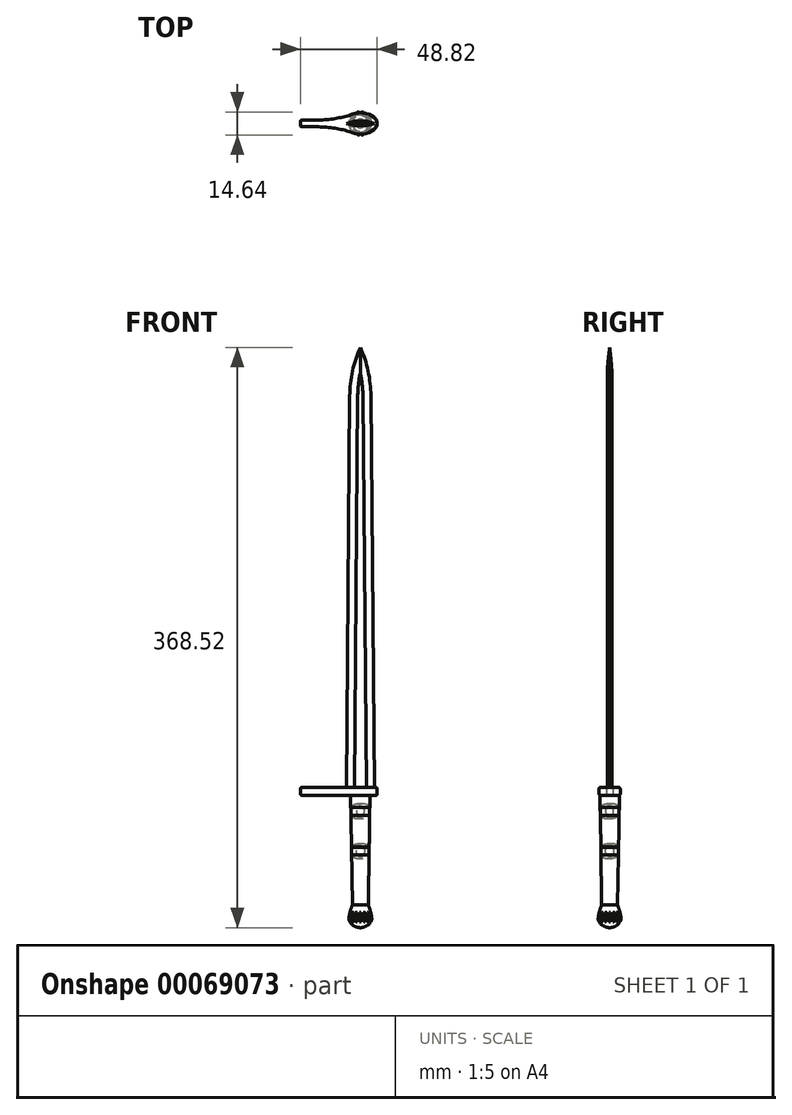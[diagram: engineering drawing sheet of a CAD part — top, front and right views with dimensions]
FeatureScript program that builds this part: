
annotation { "Feature Type Name" : "Feature", "Feature Type Description" : "" }
export const myFeature = defineFeature(function(context is Context, id is Id, definition is map)
    precondition{}
    {
        {
            var Q0;
            Q0=qCreatedBy(makeId("Right.planeOp"),FACE);
            var sketch = newSketch(context, id + "F0", { "sketchPlane" : qUnion([Q0])});
            skLineSegment(sketch, "E0", {"start": v(0, 0) * mm, "end": v(-6.1, 0) * mm});
            skLineSegment(sketch, "E1", {"start": v(0, 0) * mm, "end": v(0, -52.88) * mm});
            skLineSegment(sketch, "E2", {"start": v(0, 0) * mm, "end": v(6.1, 0) * mm});
            skPoint(sketch, "E3.end.orphan", {"position": v(-6.1, 0) * mm});
            skLineSegment(sketch, "E4", {"start": v(0, -52.88) * mm, "end": v(0, -69.72) * mm});
            skLineSegment(sketch, "E5", {"start": v(0, -69.72) * mm, "end": v(-5.08, -69.72) * mm});
            skLineSegment(sketch, "E6.MirrorCS", {"start": v(0, -69.72) * mm, "end": v(5.08, -69.72) * mm});
            skLineSegment(sketch, "E7", {"start": v(-5.08, -69.72) * mm, "end": v(-6.1, 0) * mm});
            skLineSegment(sketch, "E8", {"start": v(5.08, -69.72) * mm, "end": v(6.1, 0) * mm});
            skArc(sketch, "E9", {"start": v(-5.98, -7.62) * mm, "mid": v(-6.68, -10.11) * mm, "end": v(-5.91, -12.59) * mm});
            skLineSegment(sketch, "E10", {"start": v(-5.58, -35.4) * mm, "end": v(-13.44, -35.51) * mm});
            skArc(sketch, "E11.MirrorCS", {"start": v(-5.18, -63.18) * mm, "mid": v(-5.94, -60.7) * mm, "end": v(-5.25, -58.2) * mm});
            skLineSegment(sketch, "E12", {"start": v(-2.07, -10.05) * mm, "end": v(-5.91, -10.1) * mm});
            skLineSegment(sketch, "E13", {"start": v(-5.75, -22.75) * mm, "end": v(-5.91, -10.1) * mm});
            skPoint(sketch, "E14", {"position": v(-5.75, -22.75) * mm});
            skLineSegment(sketch, "E15", {"start": v(-5.75, -22.75) * mm, "end": v(-9.83, -22.8) * mm});
            skArc(sketch, "E16.MirrorCS", {"start": v(-5.59, -37.88) * mm, "mid": v(-6.34, -35.4) * mm, "end": v(-5.65, -32.91) * mm});
            skLineSegment(sketch, "E17", {"start": v(-5.59, -37.88) * mm, "end": v(-5.54, -37.95) * mm});
            skLineSegment(sketch, "E18", {"start": v(-5.65, -32.91) * mm, "end": v(-5.62, -32.87) * mm});
            skSolve(sketch);
        }
        {
            var Q0;
            {var subQ8=sQuery(id+"F0.wireOp",EDGE,"E0");Q0=makeQuery(id+"F0.imprint","IMPRINT",FACE,{"disambiguationData":[TD([[makeQuery(id+"F0.imprint","IMPRINT",EDGE,{"derivedFrom":subQ8}),1.0]])]});}
            var Q1;
            Q1=sQuery(id+"F0.wireOp",EDGE,"E1");
            revolve(context, id + "F1", {"entities" : qUnion([Q0]), "axis" : qUnion([Q1]), "revolveType" : RevolveType.FULL});
        }
        {
            var Q0;
            {var subQ3=sQuery(id+"F0.wireOp",EDGE,"E18");Q0=makeQuery(id+"F0.imprint","IMPRINT",FACE,{"disambiguationData":[TD([[makeQuery(id+"F0.imprint","IMPRINT",EDGE,{"derivedFrom":subQ3}),-1.0]])]});}
            var Q1;
            {var subQ3=sQuery(id+"F0.wireOp",EDGE,"E17");Q1=makeQuery(id+"F0.imprint","IMPRINT",FACE,{"disambiguationData":[TD([[makeQuery(id+"F0.imprint","IMPRINT",EDGE,{"derivedFrom":subQ3}),1.0]])]});}
            var Q2;
            {var subQ0=sQuery(id+"F0.wireOp",EDGE,"E9");Q2=makeQuery(id+"F0.imprint","IMPRINT",FACE,{"disambiguationData":[TD([[makeQuery(id+"F0.imprint","IMPRINT",EDGE,{"derivedFrom":subQ0}),1.0]])]});}
            var Q3;
            {var subQ0=sQuery(id+"F0.wireOp",EDGE,"E11.MirrorCS");Q3=makeQuery(id+"F0.imprint","IMPRINT",FACE,{"disambiguationData":[TD([[makeQuery(id+"F0.imprint","IMPRINT",EDGE,{"derivedFrom":subQ0}),-1.0]])]});}
            var Q4;
            Q4=sQuery(id+"F0.wireOp",EDGE,"E4");
            revolve(context, id + "F2", {"entities" : qUnion([Q0, Q1, Q2, Q3]), "axis" : qUnion([Q4]), "revolveType" : RevolveType.FULL});
        }
        {
            var Q0;
            Q0=makeQuery(id+"F1.opRevolve","SWEPT_FACE",FACE,{"disambiguationData":[OSD([sQuery(id+"F0.wireOp",EDGE,"E0")])]});
            var sketch = newSketch(context, id + "F3", { "sketchPlane" : qUnion([Q0])});
            skEllipse(sketch, "E19", {"center": v(0, 0) * mm, "majorRadius": 6.74 * mm, "minorRadius": 10.7 * mm, "majorAxis": v(0, 1)});
            skLineSegment(sketch, "E20", {"start": v(-10.7, 0) * mm, "end": v(-38.12, 0) * mm});
            skPoint(sketch, "E20.endSnap0", {"position": v(-10.7, 0) * mm});
            skLineSegment(sketch, "E21", {"start": v(-38.12, 0) * mm, "end": v(-38.12, 2.16) * mm});
            skLineSegment(sketch, "E22", {"start": v(-38.12, 2.16) * mm, "end": v(-27.96, 2.16) * mm});
            skArc(sketch, "E23", {"start": v(-27.96, 2.16) * mm, "mid": v(-17.38, 2.9) * mm, "end": v(-7, 5.1) * mm});
            skArc(sketch, "E24.MirrorCS", {"start": v(-27.96, -2.16) * mm, "mid": v(-17.38, -2.9) * mm, "end": v(-7, -5.1) * mm});
            skLineSegment(sketch, "E25.MirrorCS", {"start": v(-38.12, -2.16) * mm, "end": v(-27.96, -2.16) * mm});
            skLineSegment(sketch, "E26.MirrorCS", {"start": v(-38.12, 0) * mm, "end": v(-38.12, -2.16) * mm});
            skLineSegment(sketch, "E27", {"start": v(0, 0) * mm, "end": v(0, 3.03) * mm});
            skArc(sketch, "E28.MirrorCS", {"start": v(27.96, 2.16) * mm, "mid": v(17.38, 2.9) * mm, "end": v(7, 5.1) * mm});
            skArc(sketch, "E29.MirrorCS", {"start": v(27.96, -2.16) * mm, "mid": v(17.38, -2.9) * mm, "end": v(7, -5.1) * mm});
            skLineSegment(sketch, "E30.MirrorCS", {"start": v(38.12, 0) * mm, "end": v(38.12, -2.16) * mm});
            skLineSegment(sketch, "E31.MirrorCS", {"start": v(38.12, 0) * mm, "end": v(38.12, 2.16) * mm});
            skLineSegment(sketch, "E32.MirrorCS", {"start": v(38.12, 2.16) * mm, "end": v(27.96, 2.16) * mm});
            skLineSegment(sketch, "E33.MirrorCS", {"start": v(38.12, -2.16) * mm, "end": v(27.96, -2.16) * mm});
            skSolve(sketch);
        }
        {
            var Q0;
            {var subQ1=sQuery(id+"F3.wireOp",EDGE,"E20");Q0=makeQuery(id+"F3.imprint","IMPRINT",FACE,{"disambiguationData":[TD([[makeQuery(id+"F3.imprint","IMPRINT",EDGE,{"derivedFrom":subQ1}),-1.0]])]});}
            var Q1;
            {var subQ1=sQuery(id+"F3.wireOp",EDGE,"E20");Q1=makeQuery(id+"F3.imprint","IMPRINT",FACE,{"disambiguationData":[TD([[makeQuery(id+"F3.imprint","IMPRINT",EDGE,{"derivedFrom":subQ1}),1.0]])]});}
            var Q2;
            Q2=makeQuery(id+"F3.imprint","IMPRINT",FACE,{"disambiguationData":[TD([[makeQuery(id+"F3.imprint","IMPRINT",EDGE,{"derivedFrom":makeQuery(id+"F1.opRevolve","SWEPT_EDGE",EDGE,{"disambiguationData":[OSD([sQuery(id+"F0.wireOp",EDGE,"E0"),sQuery(id+"F0.wireOp",EDGE,"E7")])]})}),-1.0]])]});
            var Q3;
            {var subQ0=sQuery(id+"F3.wireOp",EDGE,"E28.MirrorCS");Q3=makeQuery(id+"F3.imprint","IMPRINT",FACE,{"disambiguationData":[TD([[makeQuery(id+"F3.imprint","IMPRINT",EDGE,{"derivedFrom":subQ0}),1.0]])]});}
            var Q4;
            Q4=makeQuery(id+"F3.imprint","IMPRINT",FACE,{"disambiguationData":[TD([[makeQuery(id+"F3.imprint","IMPRINT",EDGE,{"derivedFrom":makeQuery(id+"F1.opRevolve","SWEPT_EDGE",EDGE,{"disambiguationData":[OSD([sQuery(id+"F0.wireOp",EDGE,"E0"),sQuery(id+"F0.wireOp",EDGE,"E7")])]})}),1.0]])]});
            extrude(context, id + "F4", {"entities" : qUnion([Q0, Q1, Q2, Q3, Q4]), "depth" : 5.08 * mm});
        }
        {
            var Q0;
            Q0=makeQuery(id+"F4.opExtrude","CAP_EDGE",EDGE,{"disambiguationData":[OSD([sQuery(id+"F3.wireOp",EDGE,"E24.MirrorCS")])],"isStart":false});
            var Q1;
            Q1=makeQuery(id+"F4.opExtrude","CAP_EDGE",EDGE,{"disambiguationData":[OSD([sQuery(id+"F3.wireOp",EDGE,"E25.MirrorCS")])],"isStart":false});
            var Q2;
            Q2=makeQuery(id+"F4.opExtrude","CAP_EDGE",EDGE,{"disambiguationData":[OSD([sQuery(id+"F3.wireOp",EDGE,"E25.MirrorCS")])],"isStart":true});
            var Q3;
            Q3=makeQuery(id+"F4.opExtrude","CAP_EDGE",EDGE,{"disambiguationData":[OSD([sQuery(id+"F3.wireOp",EDGE,"E24.MirrorCS")])],"isStart":true});
            var Q4;
            Q4=makeQuery(id+"F4.opExtrude","CAP_EDGE",EDGE,{"disambiguationData":[OSD([sQuery(id+"F3.wireOp",EDGE,"E23")])],"isStart":true});
            var Q5;
            Q5=makeQuery(id+"F4.opExtrude","CAP_EDGE",EDGE,{"disambiguationData":[OSD([sQuery(id+"F3.wireOp",EDGE,"E23")])],"isStart":false});
            var Q6;
            Q6=makeQuery(id+"F4.opExtrude","CAP_EDGE",EDGE,{"disambiguationData":[OSD([sQuery(id+"F3.wireOp",EDGE,"E22")])],"isStart":false});
            var Q7;
            Q7=makeQuery(id+"F4.opExtrude","SWEPT_EDGE",EDGE,{"disambiguationData":[OSD([sQuery(id+"F3.wireOp",EDGE,"E25.MirrorCS"),sQuery(id+"F3.wireOp",EDGE,"E26.MirrorCS")])]});
            var Q8;
            Q8=makeQuery(id+"F4.opExtrude","SWEPT_EDGE",EDGE,{"disambiguationData":[OSD([sQuery(id+"F3.wireOp",EDGE,"E21"),sQuery(id+"F3.wireOp",EDGE,"E22")])]});
            var Q9;
            Q9=makeQuery(id+"F4.opExtrude","CAP_EDGE",EDGE,{"disambiguationData":[OSD([sQuery(id+"F3.wireOp",EDGE,"E21"),sQuery(id+"F3.wireOp",EDGE,"E26.MirrorCS")])],"isStart":true});
            var Q10;
            Q10=makeQuery(id+"F4.opExtrude","CAP_EDGE",EDGE,{"disambiguationData":[OSD([sQuery(id+"F3.wireOp",EDGE,"E21"),sQuery(id+"F3.wireOp",EDGE,"E26.MirrorCS")])],"isStart":false});
            var Q11;
            Q11=makeQuery(id+"F4.opExtrude","CAP_EDGE",EDGE,{"disambiguationData":[OSD([sQuery(id+"F3.wireOp",EDGE,"E29.MirrorCS")])],"isStart":false});
            var Q12;
            Q12=makeQuery(id+"F4.opExtrude","CAP_EDGE",EDGE,{"disambiguationData":[OSD([sQuery(id+"F3.wireOp",EDGE,"E29.MirrorCS")])],"isStart":true});
            var Q13;
            Q13=makeQuery(id+"F4.opExtrude","CAP_EDGE",EDGE,{"disambiguationData":[OSD([sQuery(id+"F3.wireOp",EDGE,"E28.MirrorCS")])],"isStart":false});
            var Q14;
            Q14=makeQuery(id+"F4.opExtrude","CAP_EDGE",EDGE,{"disambiguationData":[OSD([sQuery(id+"F3.wireOp",EDGE,"E28.MirrorCS")])],"isStart":true});
            var Q15;
            Q15=makeQuery(id+"F4.opExtrude","SWEPT_FACE",FACE,{"disambiguationData":[OSD([sQuery(id+"F3.wireOp",EDGE,"E30.MirrorCS"),sQuery(id+"F3.wireOp",EDGE,"E31.MirrorCS")])]});
            var Q16;
            {var subQ0=sQuery(id+"F3.wireOp",EDGE,"E19");Q16=makeQuery(id+"F4.opExtrude","SWEPT_FACE",FACE,{"disambiguationData":[OSD([subQ0]),TDD([makeQuery(id+"F3.imprint","IMPRINT",EDGE,{"disambiguationData":[TD([[makeQuery(id+"F3.imprint","INTERSECT",VERTEX,{"derivedFrom":[subQ0,sQuery(id+"F3.wireOp",EDGE,"E24.MirrorCS")]}),-1.0]])],"derivedFrom":subQ0})])]});}
            var Q17;
            {var subQ0=sQuery(id+"F3.wireOp",EDGE,"E19");Q17=makeQuery(id+"F4.opExtrude","SWEPT_FACE",FACE,{"disambiguationData":[OSD([subQ0]),TDD([makeQuery(id+"F3.imprint","IMPRINT",EDGE,{"disambiguationData":[TD([[makeQuery(id+"F3.imprint","INTERSECT",VERTEX,{"derivedFrom":[subQ0,sQuery(id+"F3.wireOp",EDGE,"E23")]}),1.0]])],"derivedFrom":subQ0})])]});}
            fillet(context, id + "F5", {"entities" : qUnion([Q0, Q1, Q2, Q3, Q4, Q5, Q6, Q7, Q8, Q9, Q10, Q11, Q12, Q13, Q14, Q15, Q16, Q17]), "radius" : 1.02 * mm, "tangentPropagation" : true, "allowEdgeOverflow" : false});
        }
        {
            var Q0;
            Q0=qCreatedBy(makeId("Front.planeOp"),FACE);
            var sketch = newSketch(context, id + "F6", { "sketchPlane" : qUnion([Q0])});
            skLineSegment(sketch, "E34.0", {"start": v(-5.08, -69.72) * mm, "end": v(5.08, -69.72) * mm});
            skArc(sketch, "E35", {"start": v(-5.08, -69.72) * mm, "mid": v(-6.56, -74.06) * mm, "end": v(-7.37, -78.58) * mm});
            skLineSegment(sketch, "E36", {"start": v(0, -69.72) * mm, "end": v(0, -75.64) * mm});
            skPoint(sketch, "E36.endSnap0", {"position": v(0, -69.72) * mm});
            skArc(sketch, "E37.MirrorCS", {"start": v(5.08, -69.72) * mm, "mid": v(6.56, -74.06) * mm, "end": v(7.37, -78.58) * mm});
            skArc(sketch, "E38", {"start": v(-7.37, -78.58) * mm, "mid": v(0, -84.04) * mm, "end": v(7.37, -78.58) * mm});
            skLineSegment(sketch, "E39", {"start": v(0, -72.68) * mm, "end": v(0, -84.04) * mm});
            skSolve(sketch);
        }
        {
            var Q0;
            {var subQ1=sQuery(id+"F6.wireOp",EDGE,"E35");Q0=makeQuery(id+"F6.imprint","IMPRINT",FACE,{"disambiguationData":[TD([[makeQuery(id+"F6.imprint","IMPRINT",EDGE,{"derivedFrom":subQ1}),1.0]])]});}
            var Q1;
            Q1=sQuery(id+"F6.wireOp",EDGE,"E39");
            revolve(context, id + "F7", {"entities" : qUnion([Q0]), "axis" : qUnion([Q1]), "revolveType" : RevolveType.FULL});
        }
        {
            var Q0;
            Q0=makeQuery(id+"F7.opRevolve","SWEPT_FACE",FACE,{"disambiguationData":[OSD([sQuery(id+"F6.wireOp",EDGE,"E34.0")])]});
            var sketch = newSketch(context, id + "F8", { "sketchPlane" : qUnion([Q0])});
            skCircle(sketch, "E40.0", {"center": v(0, 0) * mm, "radius": 7.37 * mm});
            skLineSegment(sketch, "E41", {"start": v(-0.9, 7.32) * mm, "end": v(-0.35, 6.6) * mm});
            skLineSegment(sketch, "E42", {"start": v(0, 7.32) * mm, "end": v(0, 7.11) * mm});
            skLineSegment(sketch, "E43.MirrorCS", {"start": v(0.9, 7.32) * mm, "end": v(0.35, 6.6) * mm});
            skLineSegment(sketch, "E44", {"start": v(-0.35, 6.6) * mm, "end": v(0.35, 6.6) * mm});
            skPoint(sketch, "E45.orphan", {"position": v(0.9, 7.32) * mm});
            skLineSegment(sketch, "E46.1.0", {"start": v(-1.97, 7.1) * mm, "end": v(-2.2, 6.23) * mm});
            skLineSegment(sketch, "E46.1.1", {"start": v(-2.85, 5.96) * mm, "end": v(-2.2, 6.23) * mm});
            skLineSegment(sketch, "E46.1.2", {"start": v(-3.63, 6.42) * mm, "end": v(-2.85, 5.96) * mm});
            skLineSegment(sketch, "E46.2.0", {"start": v(-4.54, 5.8) * mm, "end": v(-4.42, 4.92) * mm});
            skLineSegment(sketch, "E46.2.1", {"start": v(-4.92, 4.42) * mm, "end": v(-4.42, 4.92) * mm});
            skLineSegment(sketch, "E46.2.2", {"start": v(-5.8, 4.54) * mm, "end": v(-4.92, 4.42) * mm});
            skLineSegment(sketch, "E46.3.0", {"start": v(-6.42, 3.63) * mm, "end": v(-5.96, 2.85) * mm});
            skLineSegment(sketch, "E46.3.1", {"start": v(-6.23, 2.2) * mm, "end": v(-5.96, 2.85) * mm});
            skLineSegment(sketch, "E46.3.2", {"start": v(-7.1, 1.97) * mm, "end": v(-6.23, 2.2) * mm});
            skLineSegment(sketch, "E46.4.0", {"start": v(-7.32, 0.9) * mm, "end": v(-6.6, 0.35) * mm});
            skLineSegment(sketch, "E46.4.1", {"start": v(-6.6, -0.35) * mm, "end": v(-6.6, 0.35) * mm});
            skLineSegment(sketch, "E46.4.2", {"start": v(-7.32, -0.9) * mm, "end": v(-6.6, -0.35) * mm});
            skLineSegment(sketch, "E46.5.0", {"start": v(-7.1, -1.97) * mm, "end": v(-6.23, -2.2) * mm});
            skLineSegment(sketch, "E46.5.1", {"start": v(-5.96, -2.85) * mm, "end": v(-6.23, -2.2) * mm});
            skLineSegment(sketch, "E46.5.2", {"start": v(-6.42, -3.63) * mm, "end": v(-5.96, -2.85) * mm});
            skLineSegment(sketch, "E46.6.0", {"start": v(-5.8, -4.54) * mm, "end": v(-4.92, -4.42) * mm});
            skLineSegment(sketch, "E46.6.1", {"start": v(-4.42, -4.92) * mm, "end": v(-4.92, -4.42) * mm});
            skLineSegment(sketch, "E46.6.2", {"start": v(-4.54, -5.8) * mm, "end": v(-4.42, -4.92) * mm});
            skLineSegment(sketch, "E46.7.0", {"start": v(-3.63, -6.42) * mm, "end": v(-2.85, -5.96) * mm});
            skLineSegment(sketch, "E46.7.1", {"start": v(-2.2, -6.23) * mm, "end": v(-2.85, -5.96) * mm});
            skLineSegment(sketch, "E46.7.2", {"start": v(-1.97, -7.1) * mm, "end": v(-2.2, -6.23) * mm});
            skLineSegment(sketch, "E46.8.0", {"start": v(-0.9, -7.32) * mm, "end": v(-0.35, -6.6) * mm});
            skLineSegment(sketch, "E46.8.1", {"start": v(0.35, -6.6) * mm, "end": v(-0.35, -6.6) * mm});
            skLineSegment(sketch, "E46.8.2", {"start": v(0.9, -7.32) * mm, "end": v(0.35, -6.6) * mm});
            skLineSegment(sketch, "E46.9.0", {"start": v(1.97, -7.1) * mm, "end": v(2.2, -6.23) * mm});
            skLineSegment(sketch, "E46.9.1", {"start": v(2.85, -5.96) * mm, "end": v(2.2, -6.23) * mm});
            skLineSegment(sketch, "E46.9.2", {"start": v(3.63, -6.42) * mm, "end": v(2.85, -5.96) * mm});
            skLineSegment(sketch, "E46.10.0", {"start": v(4.54, -5.8) * mm, "end": v(4.42, -4.92) * mm});
            skLineSegment(sketch, "E46.10.1", {"start": v(4.92, -4.42) * mm, "end": v(4.42, -4.92) * mm});
            skLineSegment(sketch, "E46.10.2", {"start": v(5.8, -4.54) * mm, "end": v(4.92, -4.42) * mm});
            skLineSegment(sketch, "E46.11.0", {"start": v(6.42, -3.63) * mm, "end": v(5.96, -2.85) * mm});
            skLineSegment(sketch, "E46.11.1", {"start": v(6.23, -2.2) * mm, "end": v(5.96, -2.85) * mm});
            skLineSegment(sketch, "E46.11.2", {"start": v(7.1, -1.97) * mm, "end": v(6.23, -2.2) * mm});
            skLineSegment(sketch, "E46.12.0", {"start": v(7.32, -0.9) * mm, "end": v(6.6, -0.35) * mm});
            skLineSegment(sketch, "E46.12.1", {"start": v(6.6, 0.35) * mm, "end": v(6.6, -0.35) * mm});
            skLineSegment(sketch, "E46.12.2", {"start": v(7.32, 0.9) * mm, "end": v(6.6, 0.35) * mm});
            skLineSegment(sketch, "E46.13.0", {"start": v(7.1, 1.97) * mm, "end": v(6.23, 2.2) * mm});
            skLineSegment(sketch, "E46.13.1", {"start": v(5.96, 2.85) * mm, "end": v(6.23, 2.2) * mm});
            skLineSegment(sketch, "E46.13.2", {"start": v(6.42, 3.63) * mm, "end": v(5.96, 2.85) * mm});
            skLineSegment(sketch, "E46.14.0", {"start": v(5.8, 4.54) * mm, "end": v(4.92, 4.42) * mm});
            skLineSegment(sketch, "E46.14.1", {"start": v(4.42, 4.92) * mm, "end": v(4.92, 4.42) * mm});
            skLineSegment(sketch, "E46.14.2", {"start": v(4.54, 5.8) * mm, "end": v(4.42, 4.92) * mm});
            skLineSegment(sketch, "E46.15.0", {"start": v(3.63, 6.42) * mm, "end": v(2.85, 5.96) * mm});
            skLineSegment(sketch, "E46.15.1", {"start": v(2.2, 6.23) * mm, "end": v(2.85, 5.96) * mm});
            skLineSegment(sketch, "E46.15.2", {"start": v(1.97, 7.1) * mm, "end": v(2.2, 6.23) * mm});
            skSolve(sketch);
        }
        {
            var Q0;
            {var subQ0=sQuery(id+"F8.wireOp",EDGE,"E46.3.0");Q0=makeQuery(id+"F8.imprint","IMPRINT",FACE,{"disambiguationData":[TD([[makeQuery(id+"F8.imprint","IMPRINT",EDGE,{"derivedFrom":subQ0}),-1.0]])]});}
            var Q1;
            {var subQ0=sQuery(id+"F8.wireOp",EDGE,"E46.4.0");Q1=makeQuery(id+"F8.imprint","IMPRINT",FACE,{"disambiguationData":[TD([[makeQuery(id+"F8.imprint","IMPRINT",EDGE,{"derivedFrom":subQ0}),-1.0]])]});}
            var Q2;
            {var subQ0=sQuery(id+"F8.wireOp",EDGE,"E46.5.0");Q2=makeQuery(id+"F8.imprint","IMPRINT",FACE,{"disambiguationData":[TD([[makeQuery(id+"F8.imprint","IMPRINT",EDGE,{"derivedFrom":subQ0}),-1.0]])]});}
            var Q3;
            {var subQ0=sQuery(id+"F8.wireOp",EDGE,"E46.6.0");Q3=makeQuery(id+"F8.imprint","IMPRINT",FACE,{"disambiguationData":[TD([[makeQuery(id+"F8.imprint","IMPRINT",EDGE,{"derivedFrom":subQ0}),-1.0]])]});}
            var Q4;
            {var subQ0=sQuery(id+"F8.wireOp",EDGE,"E46.7.0");Q4=makeQuery(id+"F8.imprint","IMPRINT",FACE,{"disambiguationData":[TD([[makeQuery(id+"F8.imprint","IMPRINT",EDGE,{"derivedFrom":subQ0}),-1.0]])]});}
            var Q5;
            {var subQ0=sQuery(id+"F8.wireOp",EDGE,"E46.8.0");Q5=makeQuery(id+"F8.imprint","IMPRINT",FACE,{"disambiguationData":[TD([[makeQuery(id+"F8.imprint","IMPRINT",EDGE,{"derivedFrom":subQ0}),-1.0]])]});}
            var Q6;
            {var subQ0=sQuery(id+"F8.wireOp",EDGE,"E46.9.0");Q6=makeQuery(id+"F8.imprint","IMPRINT",FACE,{"disambiguationData":[TD([[makeQuery(id+"F8.imprint","IMPRINT",EDGE,{"derivedFrom":subQ0}),-1.0]])]});}
            var Q7;
            {var subQ0=sQuery(id+"F8.wireOp",EDGE,"E46.10.0");Q7=makeQuery(id+"F8.imprint","IMPRINT",FACE,{"disambiguationData":[TD([[makeQuery(id+"F8.imprint","IMPRINT",EDGE,{"derivedFrom":subQ0}),-1.0]])]});}
            var Q8;
            {var subQ0=sQuery(id+"F8.wireOp",EDGE,"E46.11.0");Q8=makeQuery(id+"F8.imprint","IMPRINT",FACE,{"disambiguationData":[TD([[makeQuery(id+"F8.imprint","IMPRINT",EDGE,{"derivedFrom":subQ0}),-1.0]])]});}
            var Q9;
            {var subQ0=sQuery(id+"F8.wireOp",EDGE,"E46.12.0");Q9=makeQuery(id+"F8.imprint","IMPRINT",FACE,{"disambiguationData":[TD([[makeQuery(id+"F8.imprint","IMPRINT",EDGE,{"derivedFrom":subQ0}),-1.0]])]});}
            var Q10;
            {var subQ0=sQuery(id+"F8.wireOp",EDGE,"E46.13.0");Q10=makeQuery(id+"F8.imprint","IMPRINT",FACE,{"disambiguationData":[TD([[makeQuery(id+"F8.imprint","IMPRINT",EDGE,{"derivedFrom":subQ0}),-1.0]])]});}
            var Q11;
            {var subQ0=sQuery(id+"F8.wireOp",EDGE,"E46.14.0");Q11=makeQuery(id+"F8.imprint","IMPRINT",FACE,{"disambiguationData":[TD([[makeQuery(id+"F8.imprint","IMPRINT",EDGE,{"derivedFrom":subQ0}),-1.0]])]});}
            var Q12;
            {var subQ0=sQuery(id+"F8.wireOp",EDGE,"E46.15.0");Q12=makeQuery(id+"F8.imprint","IMPRINT",FACE,{"disambiguationData":[TD([[makeQuery(id+"F8.imprint","IMPRINT",EDGE,{"derivedFrom":subQ0}),-1.0]])]});}
            var Q13;
            {var subQ0=sQuery(id+"F8.wireOp",EDGE,"E41");Q13=makeQuery(id+"F8.imprint","IMPRINT",FACE,{"disambiguationData":[TD([[makeQuery(id+"F8.imprint","IMPRINT",EDGE,{"derivedFrom":subQ0}),1.0]])]});}
            var Q14;
            {var subQ0=sQuery(id+"F8.wireOp",EDGE,"E46.1.0");Q14=makeQuery(id+"F8.imprint","IMPRINT",FACE,{"disambiguationData":[TD([[makeQuery(id+"F8.imprint","IMPRINT",EDGE,{"derivedFrom":subQ0}),-1.0]])]});}
            var Q15;
            {var subQ0=sQuery(id+"F8.wireOp",EDGE,"E46.2.0");Q15=makeQuery(id+"F8.imprint","IMPRINT",FACE,{"disambiguationData":[TD([[makeQuery(id+"F8.imprint","IMPRINT",EDGE,{"derivedFrom":subQ0}),-1.0]])]});}
            extrude(context, id + "F9", {"entities" : qUnion([Q0, Q1, Q2, Q3, Q4, Q5, Q6, Q7, Q8, Q9, Q10, Q11, Q12, Q13, Q14, Q15]), "operationType" : NewBodyOperationType.REMOVE, "oppositeDirection" : true, "depth" : 25.4 * mm});
        }
        {
            var Q0;
            Q0=qCreatedBy(makeId("Front.planeOp"),FACE);
            var sketch = newSketch(context, id + "F10", { "sketchPlane" : qUnion([Q0])});
            skFitSpline(sketch, "E47.0", {"points": [v(-6.43, 5.08) * mm, v(-2.14, 5.08) * mm, v(2.14, 5.08) * mm, v(6.43, 5.08) * mm]});
            skLineSegment(sketch, "E48.0", {"start": v(-6.43, 5.08) * mm, "end": v(-6.83, 5.08) * mm});
            skLineSegment(sketch, "E49.0", {"start": v(-27.96, 5.08) * mm, "end": v(-6.83, 5.08) * mm});
            skLineSegment(sketch, "E50.0", {"start": v(6.83, 5.08) * mm, "end": v(27.96, 5.08) * mm});
            skLineSegment(sketch, "E51.0", {"start": v(6.83, 5.08) * mm, "end": v(6.43, 5.08) * mm});
            skArc(sketch, "E52", {"start": v(-6.6, -80.31) * mm, "mid": v(0, -84.04) * mm, "end": v(6.6, -80.31) * mm});
            skPoint(sketch, "E53", {"position": v(0, 5.08) * mm});
            skPoint(sketch, "E54", {"position": v(0, -84.04) * mm});
            skLineSegment(sketch, "E55", {"start": v(0, 5.08) * mm, "end": v(0, 284.48) * mm});
            skPoint(sketch, "E56", {"position": v(-8.9, 5.08) * mm});
            skLineSegment(sketch, "E57", {"start": v(-8.9, 5.08) * mm, "end": v(-6.72, 253.77) * mm});
            skLineSegment(sketch, "E58", {"start": v(-6.83, 5.08) * mm, "end": v(-8.9, 5.08) * mm});
            skArc(sketch, "E59", {"start": v(0, 284.48) * mm, "mid": v(-4.95, 269.47) * mm, "end": v(-6.72, 253.77) * mm});
            skLineSegment(sketch, "E60.MirrorCS", {"start": v(8.9, 5.08) * mm, "end": v(6.72, 253.77) * mm});
            skArc(sketch, "E61.MirrorCS", {"start": v(0, 284.48) * mm, "mid": v(4.95, 269.47) * mm, "end": v(6.72, 253.77) * mm});
            skSolve(sketch);
        }
        {
            var Q0;
            Q0 = qSketchRegion(id + "F10", true);
            extrude(context, id + "F11", {"entities" : qUnion([Q0]), "endBound" : BoundingType.SYMMETRIC, "depth" : 3.05 * mm});
        }
        {
            var Q0;
            Q0=makeQuery(id+"F11.opExtrude","CAP_EDGE",EDGE,{"disambiguationData":[OSD([sQuery(id+"F10.wireOp",EDGE,"E57")])],"isStart":false});
            var Q1;
            Q1=makeQuery(id+"F11.opExtrude","CAP_EDGE",EDGE,{"disambiguationData":[OSD([sQuery(id+"F10.wireOp",EDGE,"E60.MirrorCS")])],"isStart":false});
            chamfer(context, id + "F12", {"entities" : qUnion([Q0, Q1]), "chamferType" : ChamferType.TWO_OFFSETS, "width1" : 1.52 * mm, "oppositeDirection" : false, "width2" : 5.08 * mm, "tangentPropagation" : true});
        }
        {
            var Q0;
            Q0=makeQuery(id+"F11.opExtrude","CAP_EDGE",EDGE,{"disambiguationData":[OSD([sQuery(id+"F10.wireOp",EDGE,"E60.MirrorCS")])],"isStart":true});
            var Q1;
            Q1=makeQuery(id+"F11.opExtrude","CAP_EDGE",EDGE,{"disambiguationData":[OSD([sQuery(id+"F10.wireOp",EDGE,"E57")])],"isStart":true});
            chamfer(context, id + "F13", {"entities" : qUnion([Q0, Q1]), "chamferType" : ChamferType.TWO_OFFSETS, "width1" : 1.52 * mm, "oppositeDirection" : false, "width2" : 5.08 * mm, "tangentPropagation" : true});
        }
        {
            var Q0;
            Q0=qCreatedBy(makeId("Front.planeOp"),FACE);
            var sketch = newSketch(context, id + "F14", { "sketchPlane" : qUnion([Q0])});
            skLineSegment(sketch, "E62.0", {"start": v(-3.8, 5.08) * mm, "end": v(-6.43, 5.08) * mm});
            skFitSpline(sketch, "E63.0", {"points": [v(-6.43, 5.08) * mm, v(-2.14, 5.08) * mm, v(2.14, 5.08) * mm, v(6.43, 5.08) * mm]});
            skLineSegment(sketch, "E64.0", {"start": v(6.43, 5.08) * mm, "end": v(3.8, 5.08) * mm});
            skLineSegment(sketch, "E65", {"start": v(-5.55, 5.08) * mm, "end": v(-3.57, -75.16) * mm});
            skLineSegment(sketch, "E66", {"start": v(0, 5.08) * mm, "end": v(0, -77.77) * mm});
            skLineSegment(sketch, "E67.MirrorCS", {"start": v(5.55, 5.08) * mm, "end": v(3.57, -75.16) * mm});
            skLineSegment(sketch, "E68", {"start": v(-3.57, -75.16) * mm, "end": v(3.57, -75.16) * mm});
            skSolve(sketch);
        }
        {
            var Q0;
            Q0 = qSketchRegion(id + "F14", true);
            extrude(context, id + "F15", {"entities" : qUnion([Q0]), "operationType" : NewBodyOperationType.REMOVE, "endBound" : BoundingType.SYMMETRIC, "oppositeDirection" : true, "depth" : 2.03 * mm});
        }
        {
            var Q0;
            {var subQ5=sQuery(id+"F14.wireOp",EDGE,"E65");Q0=makeQuery(id+"F14.imprint","IMPRINT",FACE,{"disambiguationData":[TD([[makeQuery(id+"F14.imprint","IMPRINT",EDGE,{"derivedFrom":subQ5}),1.0]])]});}
            var Q1;
            {var subQ7=sQuery(id+"F14.wireOp",EDGE,"E67.MirrorCS");Q1=makeQuery(id+"F14.imprint","IMPRINT",FACE,{"disambiguationData":[TD([[makeQuery(id+"F14.imprint","IMPRINT",EDGE,{"derivedFrom":subQ7}),-1.0]])]});}
            extrude(context, id + "F16", {"entities" : qUnion([Q0, Q1]), "operationType" : NewBodyOperationType.ADD, "endBound" : BoundingType.SYMMETRIC, "depth" : 2.03 * mm});
        }
    });
